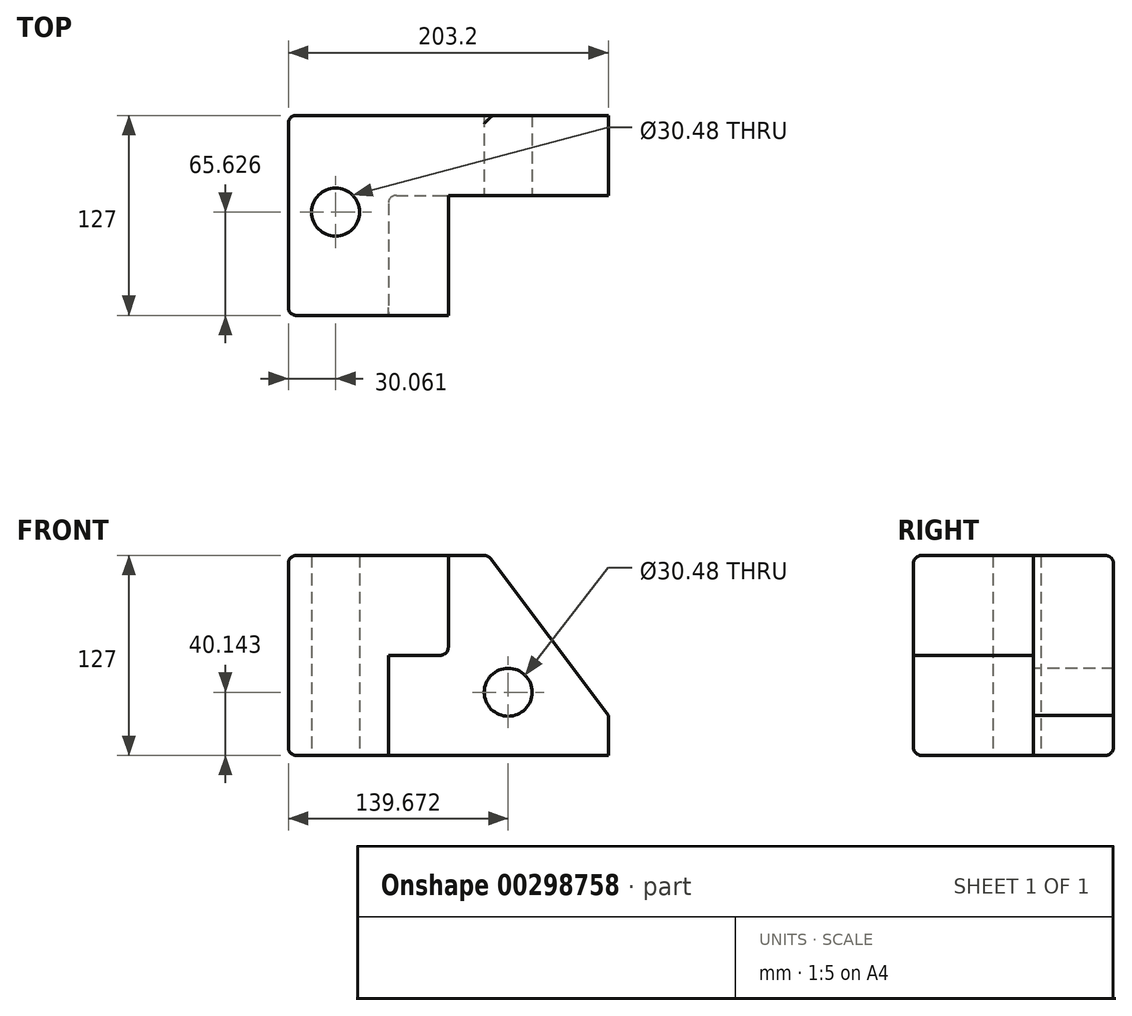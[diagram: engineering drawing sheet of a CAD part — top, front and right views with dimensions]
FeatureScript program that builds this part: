
annotation { "Feature Type Name" : "Feature", "Feature Type Description" : "" }
export const myFeature = defineFeature(function(context is Context, id is Id, definition is map)
    precondition{}
    {
        {
            var Q0;
            Q0=qCreatedBy(makeId("Front.planeOp"),FACE);
            var sketch = newSketch(context, id + "F0", { "sketchPlane" : qUnion([Q0])});
            skLineSegment(sketch, "E0.bottom", {"start": v(-123.54, 63.38) * mm, "end": v(79.66, 63.38) * mm});
            skLineSegment(sketch, "E0.top", {"start": v(-123.54, -63.62) * mm, "end": v(79.66, -63.62) * mm});
            skLineSegment(sketch, "E0.left", {"start": v(-123.54, 63.38) * mm, "end": v(-123.54, -63.62) * mm});
            skLineSegment(sketch, "E0.right", {"start": v(79.66, 63.38) * mm, "end": v(79.66, -63.62) * mm});
            skSolve(sketch);
        }
        {
            var Q0;
            Q0=makeQuery(id+"F0.imprint","IMPRINT",FACE,{"disambiguationData":[TD([[makeQuery(id+"F0.imprint","IMPRINT",EDGE,{"derivedFrom":sQuery(id+"F0.wireOp",EDGE,"E0.bottom")}),-1.0]])]});
            extrude(context, id + "F1", {"entities" : qUnion([Q0]), "depth" : 127 * mm});
        }
        {
            var Q0;
            Q0=makeQuery(id+"F1.opExtrude","CAP_FACE",FACE,{"disambiguationData":[OSD([sQuery(id+"F0.wireOp",EDGE,"E0.bottom"),sQuery(id+"F0.wireOp",EDGE,"E0.top"),sQuery(id+"F0.wireOp",EDGE,"E0.left"),sQuery(id+"F0.wireOp",EDGE,"E0.right")])],"isStart":false});
            var sketch = newSketch(context, id + "F2", { "sketchPlane" : qUnion([Q0])});
            skLineSegment(sketch, "E1", {"start": v(-123.54, 63.38) * mm, "end": v(-123.54, -63.62) * mm});
            skLineSegment(sketch, "E2", {"start": v(-123.54, -63.62) * mm, "end": v(-60.04, -63.62) * mm});
            skLineSegment(sketch, "E3", {"start": v(-60.04, -63.62) * mm, "end": v(-60.04, 0) * mm});
            skLineSegment(sketch, "E4", {"start": v(-60.04, 0) * mm, "end": v(-21.94, 0) * mm});
            skLineSegment(sketch, "E5", {"start": v(-21.94, 0) * mm, "end": v(-21.94, 63.38) * mm});
            skLineSegment(sketch, "E6", {"start": v(-21.94, 63.38) * mm, "end": v(-123.54, 63.38) * mm});
            skSolve(sketch);
        }
        {
            var Q0;
            {var subQ3=sQuery(id+"F2.wireOp",EDGE,"E3");Q0=makeQuery(id+"F2.imprint","IMPRINT",FACE,{"disambiguationData":[TD([[makeQuery(id+"F2.imprint","IMPRINT",EDGE,{"derivedFrom":subQ3}),-1.0]])]});}
            extrude(context, id + "F3", {"entities" : qUnion([Q0]), "operationType" : NewBodyOperationType.REMOVE, "oppositeDirection" : true, "depth" : 76.2 * mm});
        }
        {
            var Q0;
            Q0=makeQuery(id+"F1.opExtrude","SWEPT_EDGE",EDGE,{"disambiguationData":[OSD([sQuery(id+"F0.wireOp",EDGE,"E0.bottom"),sQuery(id+"F0.wireOp",EDGE,"E0.right")])]});
            chamfer(context, id + "F4", {"entities" : qUnion([Q0]), "chamferType" : ChamferType.TWO_OFFSETS, "width1" : 76.2 * mm, "oppositeDirection" : false, "width2" : 101.6 * mm, "tangentPropagation" : true});
        }
        {
            var Q0;
            Q0=makeQuery(id+"F1.opExtrude","CAP_EDGE",EDGE,{"disambiguationData":[OSD([sQuery(id+"F0.wireOp",EDGE,"E0.bottom")])],"isStart":false});
            var Q1;
            Q1=makeQuery(id+"F3.boolean.opBoolean","COPY",EDGE,{"derivedFrom":makeQuery(id+"F3.opExtrude","SWEPT_EDGE",EDGE,{"disambiguationData":[OSD([sQuery(id+"F0.wireOp",EDGE,"E0.bottom"),sQuery(id+"F2.wireOp",EDGE,"E5"),sQuery(id+"F2.wireOp",EDGE,"E6")])]})});
            var Q2;
            Q2=makeQuery(id+"F3.boolean.opBoolean","COPY",EDGE,{"derivedFrom":makeQuery(id+"F3.opExtrude","CAP_EDGE",EDGE,{"disambiguationData":[OSD([sQuery(id+"F2.wireOp",EDGE,"E4")])],"isStart":true})});
            var Q3;
            Q3=makeQuery(id+"F3.boolean.opBoolean","COPY",EDGE,{"derivedFrom":makeQuery(id+"F3.opExtrude","SWEPT_EDGE",EDGE,{"disambiguationData":[OSD([sQuery(id+"F2.wireOp",EDGE,"E4"),sQuery(id+"F2.wireOp",EDGE,"E5")])]})});
            var Q4;
            Q4=makeQuery(id+"F3.boolean.opBoolean","COPY",EDGE,{"derivedFrom":makeQuery(id+"F3.opExtrude","CAP_EDGE",EDGE,{"disambiguationData":[OSD([sQuery(id+"F2.wireOp",EDGE,"E5")])],"isStart":true})});
            var Q5;
            Q5=makeQuery(id+"F3.boolean.opBoolean","COPY",EDGE,{"derivedFrom":makeQuery(id+"F3.opExtrude","CAP_EDGE",EDGE,{"disambiguationData":[OSD([sQuery(id+"F2.wireOp",EDGE,"E3")])],"isStart":true})});
            var Q6;
            Q6=makeQuery(id+"F3.boolean.opBoolean","COPY",EDGE,{"derivedFrom":makeQuery(id+"F3.opExtrude","CAP_EDGE",EDGE,{"disambiguationData":[OSD([sQuery(id+"F2.wireOp",EDGE,"E3")])],"isStart":false})});
            var Q7;
            Q7=makeQuery(id+"F3.boolean.opBoolean","COPY",EDGE,{"derivedFrom":makeQuery(id+"F3.opExtrude","CAP_EDGE",EDGE,{"disambiguationData":[OSD([sQuery(id+"F0.wireOp",EDGE,"E0.top")])],"isStart":false})});
            var Q8;
            {var subQ0=sQuery(id+"F0.wireOp",EDGE,"E0.bottom");Q8=makeQuery(id+"F4.opChamfer","BLEND_EDGE",EDGE,{"blendedFrom":[makeQuery(id+"F1.opExtrude","SWEPT_EDGE",EDGE,{"disambiguationData":[OSD([subQ0,sQuery(id+"F0.wireOp",EDGE,"E0.right")])]}),makeQuery(id+"F1.opExtrude","SWEPT_FACE",FACE,{"disambiguationData":[OSD([subQ0])]})],"blendedInto":[makeQuery(id+"F1.opExtrude","SWEPT_FACE",FACE,{"disambiguationData":[OSD([subQ0])]})]});}
            var Q9;
            Q9=makeQuery(id+"F3.boolean.opBoolean","COPY",EDGE,{"derivedFrom":makeQuery(id+"F3.opExtrude","CAP_EDGE",EDGE,{"disambiguationData":[OSD([sQuery(id+"F0.wireOp",EDGE,"E0.bottom")])],"isStart":false})});
            var Q10;
            Q10=makeQuery(id+"F1.opExtrude","CAP_EDGE",EDGE,{"disambiguationData":[OSD([sQuery(id+"F0.wireOp",EDGE,"E0.left")])],"isStart":false});
            var Q11;
            Q11=makeQuery(id+"F1.opExtrude","CAP_EDGE",EDGE,{"disambiguationData":[OSD([sQuery(id+"F0.wireOp",EDGE,"E0.left")])],"isStart":true});
            var Q12;
            Q12=makeQuery(id+"F1.opExtrude","SWEPT_EDGE",EDGE,{"disambiguationData":[OSD([sQuery(id+"F0.wireOp",EDGE,"E0.top"),sQuery(id+"F0.wireOp",EDGE,"E0.left")])]});
            var Q13;
            Q13=makeQuery(id+"F1.opExtrude","SWEPT_EDGE",EDGE,{"disambiguationData":[OSD([sQuery(id+"F0.wireOp",EDGE,"E0.bottom"),sQuery(id+"F0.wireOp",EDGE,"E0.left")])]});
            var Q14;
            Q14=makeQuery(id+"F1.opExtrude","CAP_EDGE",EDGE,{"disambiguationData":[OSD([sQuery(id+"F0.wireOp",EDGE,"E0.top")])],"isStart":true});
            var Q15;
            Q15=makeQuery(id+"F1.opExtrude","CAP_EDGE",EDGE,{"disambiguationData":[OSD([sQuery(id+"F0.wireOp",EDGE,"E0.bottom")])],"isStart":true});
            var Q16;
            Q16=makeQuery(id+"F1.opExtrude","CAP_EDGE",EDGE,{"disambiguationData":[OSD([sQuery(id+"F0.wireOp",EDGE,"E0.top")])],"isStart":false});
            fillet(context, id + "F5", {"entities" : qUnion([Q0, Q1, Q2, Q3, Q4, Q5, Q6, Q7, Q8, Q9, Q10, Q11, Q12, Q13, Q14, Q15, Q16]), "radius" : 5.08 * mm, "tangentPropagation" : true, "allowEdgeOverflow" : false});
        }
        {
            var Q0;
            Q0=makeQuery(id+"F3.boolean.opBoolean","COPY",FACE,{"derivedFrom":makeQuery(id+"F3.opExtrude","CAP_FACE",FACE,{"disambiguationData":[OSD([sQuery(id+"F0.wireOp",EDGE,"E0.bottom"),sQuery(id+"F0.wireOp",EDGE,"E0.top"),sQuery(id+"F0.wireOp",EDGE,"E0.right"),sQuery(id+"F2.wireOp",EDGE,"E3"),sQuery(id+"F2.wireOp",EDGE,"E4"),sQuery(id+"F2.wireOp",EDGE,"E5")])],"isStart":false})});
            var sketch = newSketch(context, id + "F6", { "sketchPlane" : qUnion([Q0])});
            skCircle(sketch, "E7", {"center": v(16.13, -23.48) * mm, "radius": 15.24 * mm});
            skSolve(sketch);
        }
        {
            var Q0;
            Q0=makeQuery(id+"F6.imprint","IMPRINT",FACE,{"disambiguationData":[TD([[makeQuery(id+"F6.imprint","IMPRINT",EDGE,{"derivedFrom":sQuery(id+"F6.wireOp",EDGE,"E7")}),1.0]])]});
            var Q1;
            Q1=makeQuery(id+"F1.opExtrude","CAP_FACE",FACE,{"disambiguationData":[OSD([sQuery(id+"F0.wireOp",EDGE,"E0.bottom"),sQuery(id+"F0.wireOp",EDGE,"E0.top"),sQuery(id+"F0.wireOp",EDGE,"E0.left"),sQuery(id+"F0.wireOp",EDGE,"E0.right")])],"isStart":true});
            extrude(context, id + "F7", {"entities" : qUnion([Q0]), "operationType" : NewBodyOperationType.REMOVE, "endBound" : BoundingType.UP_TO_SURFACE, "oppositeDirection" : true, "endBoundEntityFace" : qUnion([Q1]), "depth" : 25.4 * mm});
        }
        {
            var Q0;
            Q0=makeQuery(id+"F1.opExtrude","SWEPT_FACE",FACE,{"disambiguationData":[OSD([sQuery(id+"F0.wireOp",EDGE,"E0.top")])]});
            var sketch = newSketch(context, id + "F8", { "sketchPlane" : qUnion([Q0])});
            skCircle(sketch, "E8", {"center": v(-93.48, 61.37) * mm, "radius": 15.24 * mm});
            skSolve(sketch);
        }
        {
            var Q0;
            Q0=makeQuery(id+"F8.imprint","IMPRINT",FACE,{"disambiguationData":[TD([[makeQuery(id+"F8.imprint","IMPRINT",EDGE,{"derivedFrom":sQuery(id+"F8.wireOp",EDGE,"E8")}),1.0]])]});
            var Q1;
            Q1=makeQuery(id+"F1.opExtrude","SWEPT_FACE",FACE,{"disambiguationData":[OSD([sQuery(id+"F0.wireOp",EDGE,"E0.bottom")])]});
            extrude(context, id + "F9", {"entities" : qUnion([Q0]), "operationType" : NewBodyOperationType.REMOVE, "endBound" : BoundingType.UP_TO_SURFACE, "oppositeDirection" : true, "endBoundEntityFace" : qUnion([Q1]), "depth" : 25.4 * mm});
        }
    });
